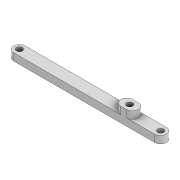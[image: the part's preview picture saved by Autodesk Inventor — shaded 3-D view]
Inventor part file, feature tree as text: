
AUTODESK INVENTOR PART (.ipt)
format: ipt  version: 2022 (Build 260153000, 153)  size: 115,200 bytes
history: native  units: mm
features: extrude x2, sketch x2, projected_geometry x1
ambient origin geometry x8: Origin, YZ Plane, XZ Plane, XY Plane, X Axis, Y Axis, Z Axis, Center Point
bodies: Solid1 (feature_tree)
feature tree (5):
  extrude  "Extrusion1"  Depth=8.0mm
  extrude  "Extrusion7"  Depth=5.0mm TaperAngle=0.0deg
  sketch  "Sketch1"  dims[d0=96.842mm d1=8.0mm]
  sketch  "Sketch4"  dims[d2=4.2mm d4=5.0mm d5=0.0mm d10=4.2mm d28=4.2mm d29=75.611mm d30=8.0mm d31=8.0mm d32=8.0mm d33=2.0mm d34=2.0mm d35=5.0mm d36=0.0mm]
  projected_geometry  "Projected Loop3"
